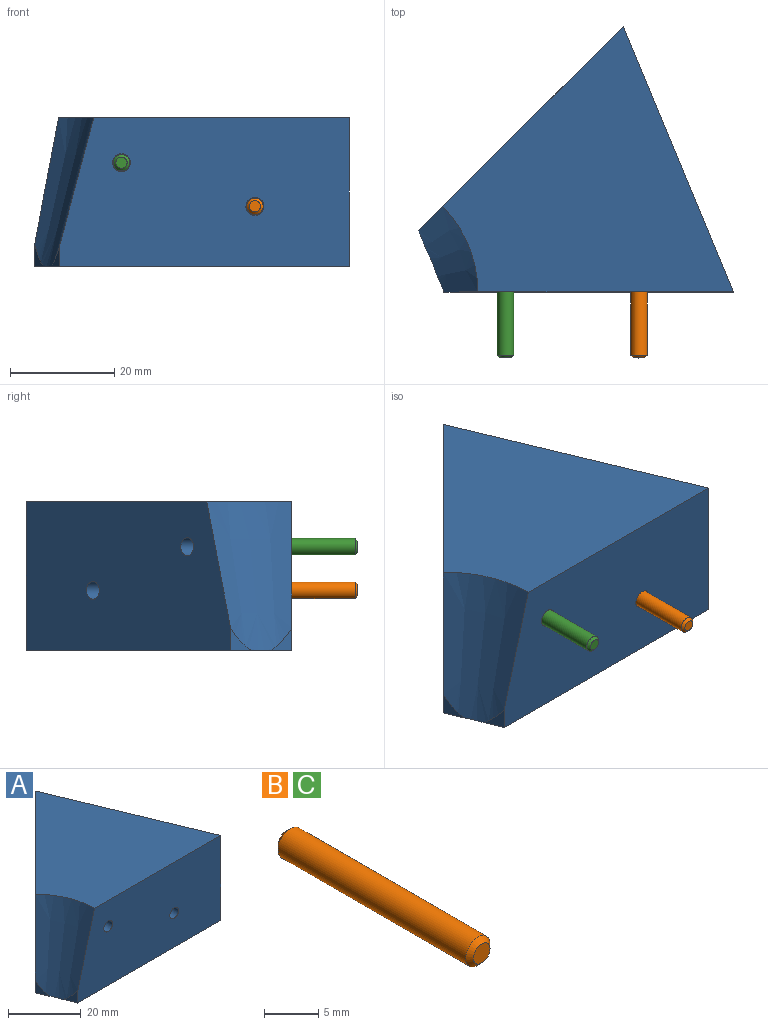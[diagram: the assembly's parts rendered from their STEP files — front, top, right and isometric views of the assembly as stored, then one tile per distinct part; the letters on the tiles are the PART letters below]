
ASSEMBLY  parts=3 mates=2
PART A: 16 faces, bbox 61.3x51.1x28.6 mm
  f0: plane 39.33x39.33mm, normal (-0.71,0.71,0), area 1491.5mm2, adj f2,f3,f5,f6,f12,f14,f15
  f1: plane 4.27x4.09mm, normal (-0.92,-0.38,0), area 7.9mm2, adj f4,f6,f15
  f2: plane 4.27x4.09mm, normal (-0.92,-0.38,0), area 7.9mm2, adj f0,f6,f15
  f3: plane 55.89x51.09mm, normal (0,0,1), area 1635.3mm2, adj f0,f4,f5,f15
  f4: plane 55.62x28.58mm, normal (0,-1,0), area 1491.5mm2, adj f1,f3,f5,f6,f8,f10,f15
  f5: plane 51.09x28.58mm, normal (0.92,0.38,0), area 1580.2mm2, adj f0,f3,f4,f6
  f6: plane 60.49x51.09mm, normal (0,0,-1), area 1747.5mm2, adj f0,f1,f2,f4,f5,f15
  f7: cone r=0mm half-angle=59deg, axis (0,-1,0), area 10.9mm2, adj f8
  f8: cylinder r=1.73mm len=6.73mm, axis (0,-1,0), area 73mm2, adj f4,f7
  f9: cone r=0mm half-angle=59deg, axis (0,-1,0), area 10.9mm2, adj f10
  f10: cylinder r=1.73mm len=6.73mm, axis (0,-1,0), area 73mm2, adj f4,f9
  f11: cone r=0mm half-angle=59deg, axis (-0.71,0.71,0), area 10.9mm2, adj f12
  f12: cylinder r=1.73mm len=7.2mm, axis (-0.71,0.71,0), area 73mm2, adj f0,f11
  f13: cone r=0mm half-angle=59deg, axis (-0.71,0.71,0), area 10.9mm2, adj f14
  f14: cylinder r=1.73mm len=7.2mm, axis (-0.71,0.71,0), area 73mm2, adj f0,f13
  f15: cone r=23.14mm half-angle=15deg, axis (0,0,1), area 433.6mm2, adj f0,f1,f2,f3,f4,f6
PART B: 5 faces, bbox 3.2x25.4x3.2 mm
  f0: cylinder r=1.59mm len=24.38mm, axis (0,-1,0), area 243.2mm2, adj f3,f4
  f1: plane 2.16x2.16mm, normal (0,1,0), area 3.7mm2, adj f3
  f2: plane 2.16x2.16mm, normal (0,-1,0), area 3.7mm2, adj f4
  f3: cone r=1.59mm half-angle=45deg, axis (0,-1,0), area 6mm2, adj f0,f1
  f4: cone r=1.08mm half-angle=45deg, axis (0,1,0), area 6mm2, adj f0,f2
PART C: same geometry as B
PLACE A at identity
PLACE B t=(54.1,-12.7,46.74)mm
PLACE C t=(28.45,-12.7,55.12)mm
MATE fastened C.f0 <-> A.f9  axis (0,-1,0) through (28.45,0,55.12)mm
MATE fastened B.f0 <-> A.f7  axis (0,-1,0) through (54.1,0,46.74)mm
